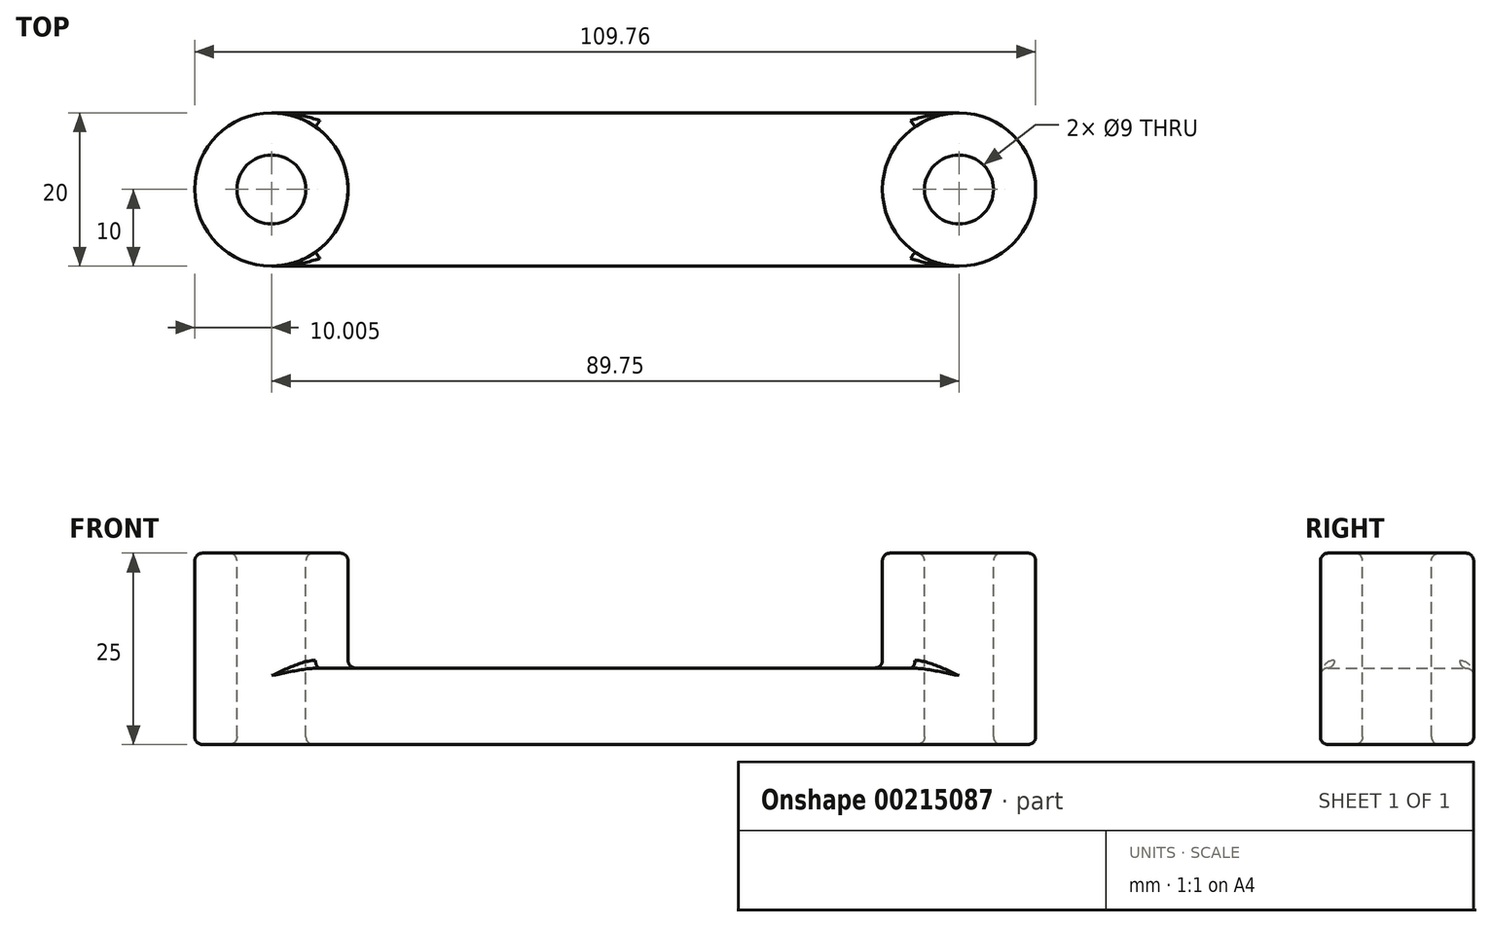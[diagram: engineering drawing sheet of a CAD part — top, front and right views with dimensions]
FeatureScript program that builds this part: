
annotation { "Feature Type Name" : "Feature", "Feature Type Description" : "" }
export const myFeature = defineFeature(function(context is Context, id is Id, definition is map)
    precondition{}
    {
        {
            var Q0;
            Q0=qCreatedBy(makeId("Top.planeOp"),FACE);
            var sketch = newSketch(context, id + "F0", { "sketchPlane" : qUnion([Q0])});
            skLineSegment(sketch, "E0", {"start": v(0, 0) * mm, "end": v(44.88, 0) * mm, "construction": true});
            skLineSegment(sketch, "E1", {"start": v(0, 0) * mm, "end": v(-44.88, 0) * mm, "construction": true});
            skCircle(sketch, "E2", {"center": v(-44.88, 0) * mm, "radius": 4.5 * mm});
            skCircle(sketch, "E3", {"center": v(44.88, 0) * mm, "radius": 4.5 * mm});
            skCircle(sketch, "E4", {"center": v(-44.88, 0) * mm, "radius": 10 * mm});
            skCircle(sketch, "E5", {"center": v(44.88, 0) * mm, "radius": 10 * mm});
            skLineSegment(sketch, "E6", {"start": v(-44.88, 10) * mm, "end": v(44.88, 10) * mm});
            skLineSegment(sketch, "E7", {"start": v(-44.88, -10) * mm, "end": v(44.88, -10) * mm});
            skSolve(sketch);
        }
        {
            var Q0;
            Q0=qSketchRegion(id+"F0",true);
            extrude(context, id + "F1", {"entities" : qUnion([Q0]), "oppositeDirection" : true, "depth" : 10 * mm});
        }
        {
            var Q0;
            Q0=makeQuery(id+"F0.imprint","IMPRINT",FACE,{"disambiguationData":[TD([[makeQuery(id+"F0.imprint","IMPRINT",EDGE,{"derivedFrom":sQuery(id+"F0.wireOp",EDGE,"E2")}),-1.0]])]});
            var Q1;
            Q1=makeQuery(id+"F0.imprint","IMPRINT",FACE,{"disambiguationData":[TD([[makeQuery(id+"F0.imprint","IMPRINT",EDGE,{"derivedFrom":sQuery(id+"F0.wireOp",EDGE,"E3")}),-1.0]])]});
            extrude(context, id + "F2", {"entities" : qUnion([Q0, Q1]), "operationType" : NewBodyOperationType.ADD, "depth" : 15 * mm});
        }
        {
            var Q0;
            Q0=makeQuery(id+"F2.opExtrude","CAP_FACE",FACE,{"disambiguationData":[OSD([sQuery(id+"F0.wireOp",EDGE,"E2"),sQuery(id+"F0.wireOp",EDGE,"E4")])],"isStart":false});
            var Q1;
            Q1=makeQuery(id+"F1.opExtrude","CAP_FACE",FACE,{"disambiguationData":[OSD([sQuery(id+"F0.wireOp",EDGE,"E2"),sQuery(id+"F0.wireOp",EDGE,"E3"),sQuery(id+"F0.wireOp",EDGE,"E4"),sQuery(id+"F0.wireOp",EDGE,"E5"),sQuery(id+"F0.wireOp",EDGE,"E6"),sQuery(id+"F0.wireOp",EDGE,"E7")])],"isStart":true});
            var Q2;
            Q2=makeQuery(id+"F2.opExtrude","CAP_FACE",FACE,{"disambiguationData":[OSD([sQuery(id+"F0.wireOp",EDGE,"E3"),sQuery(id+"F0.wireOp",EDGE,"E5")])],"isStart":false});
            var Q3;
            Q3=makeQuery(id+"F1.opExtrude","CAP_FACE",FACE,{"disambiguationData":[OSD([sQuery(id+"F0.wireOp",EDGE,"E2"),sQuery(id+"F0.wireOp",EDGE,"E3"),sQuery(id+"F0.wireOp",EDGE,"E4"),sQuery(id+"F0.wireOp",EDGE,"E5"),sQuery(id+"F0.wireOp",EDGE,"E6"),sQuery(id+"F0.wireOp",EDGE,"E7")])],"isStart":false});
            fillet(context, id + "F3", {"entities" : qUnion([Q0, Q1, Q2, Q3]), "radius" : 1 * mm, "tangentPropagation" : true, "allowEdgeOverflow" : false});
        }
    });
